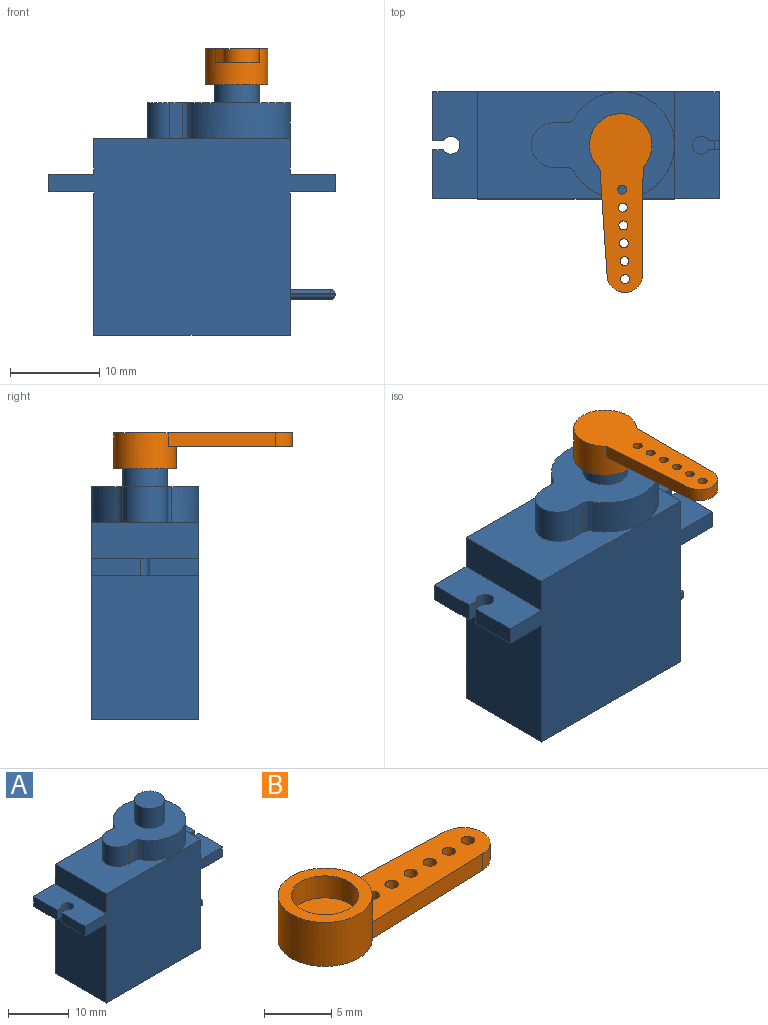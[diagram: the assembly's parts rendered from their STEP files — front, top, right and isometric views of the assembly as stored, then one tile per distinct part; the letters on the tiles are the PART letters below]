
ASSEMBLY  parts=2 mates=1
PART A: 50 faces, bbox 32x12x30 mm
  f0: plane 5.5x2mm, normal (1,0,0), area 11mm2, adj f8,f24,f25,f30
  f1: plane 5.5x2mm, normal (-1,0,0), area 11mm2, adj f2,f3,f8,f28
  f2: plane 12x5mm, normal (0,0,1), area 55.8mm2, adj f1,f8,f9,f10,f26,f27,f28,f29
  f3: plane 12x5mm, normal (0,0,-1), area 55.8mm2, adj f1,f4,f8,f10,f26,f27,f28,f29
  f4: plane 16x12mm, normal (-1,0,0), area 192mm2, adj f3,f8,f10,f13
  f5: plane 16x12mm, normal (1,0,0), area 188.4mm2, adj f8,f10,f13,f24,f33,f34,f35,f36
  f6: plane 16x12mm, normal (0,0,1), area 117.1mm2, adj f8,f9,f10,f14,f15,f16,f17,f21
  f7: plane 6x6mm, normal (0,0,1), area 7.7mm2, adj f10,f11,f14
  f8: plane 32x22mm, normal (0,1,0), area 504mm2, adj f0,f1,f2,f3,f4,f5,f6,f9
  f9: plane 12x4mm, normal (-1,0,0), area 48mm2, adj f2,f6,f8,f10
  f10: plane 32x22mm, normal (0,-1,0), area 504mm2, adj f2,f3,f4,f5,f6,f7,f9,f11
  f11: plane 12x4mm, normal (1,0,0), area 48mm2, adj f7,f8,f10,f12,f25
  f12: plane 6x6mm, normal (0,0,1), area 7.7mm2, adj f8,f11,f14
  f13: plane 22x12mm, normal (0,0,-1), area 264mm2, adj f4,f5,f8,f10
  f14: cylinder r=6mm len=12mm, axis (0,0,-1), area 125.7mm2, adj f6,f7,f12,f18,f21,f22
  f15: plane 4x1.44mm, normal (0,1,0), area 5.8mm2, adj f6,f16,f18,f21
  f16: cylinder r=2.5mm len=5mm, axis (0,0,-1), area 31.4mm2, adj f6,f15,f17,f18
  f17: plane 4x1.44mm, normal (0,-1,0), area 5.8mm2, adj f6,f16,f18,f22
  f18: plane 16x12mm, normal (0,0,1), area 111.8mm2, adj f14,f15,f16,f17,f19,f21,f22
  f19: cylinder r=2.5mm len=5mm, axis (0,0,-1), area 62.8mm2, adj f18,f20
  f20: plane 5x5mm, normal (0,0,1), area 19.6mm2, adj f19
  f21: cylinder r=1mm len=4mm, axis (0,0,-1), area 4.2mm2, adj f6,f14,f15,f18
  f22: cylinder r=1mm len=4mm, axis (0,0,-1), area 4.2mm2, adj f6,f14,f17,f18
  f23: plane 5.5x2mm, normal (1,0,0), area 11mm2, adj f10,f24,f25,f31
  f24: plane 12x5mm, normal (0,0,-1), area 55.8mm2, adj f0,f5,f8,f10,f23,f30,f31,f32
  f25: plane 12x5mm, normal (0,0,1), area 55.8mm2, adj f0,f8,f10,f11,f23,f30,f31,f32
  f26: plane 5.5x2mm, normal (-1,0,0), area 11mm2, adj f2,f3,f10,f29
  f27: cylinder r=1mm len=2mm, axis (0,0,1), area 10.5mm2, adj f2,f3,f28,f29
  f28: plane 2x1.13mm, normal (0,-1,0), area 2.3mm2, adj f1,f2,f3,f27
  f29: plane 2x1.13mm, normal (0,1,0), area 2.3mm2, adj f2,f3,f26,f27
  f30: plane 2x1.13mm, normal (0,-1,0), area 2.3mm2, adj f0,f24,f25,f32
  f31: plane 2x1.13mm, normal (0,1,0), area 2.3mm2, adj f23,f24,f25,f32
  f32: cylinder r=1mm len=2mm, axis (0,0,1), area 10.5mm2, adj f24,f25,f30,f31
  f33: plane 4.5x2.5mm, normal (0,0,1), area 11.2mm2, adj f5,f40,f46,f49
  f34: plane 4.5x0.1mm, normal (0,-1,0), area 0.5mm2, adj f5,f43,f47,f49
  f35: plane 4.5x2.5mm, normal (0,0,-1), area 11.2mm2, adj f5,f38,f42,f43
  f36: plane 4.5x0.1mm, normal (0,1,0), area 0.5mm2, adj f5,f38,f40,f41
  f37: plane 2.5x0.1mm, normal (1,0,0), area 0.3mm2, adj f41,f42,f46,f47
  f38: cylinder r=0.5mm len=4.5mm, axis (1,0,0), area 3.5mm2, adj f5,f35,f36,f39
  f39: sphere r=0.5mm, area 0.4mm2, adj f38,f41,f42
  f40: cylinder r=0.5mm len=4.5mm, axis (-1,0,0), area 3.5mm2, adj f5,f33,f36,f44
  f41: cylinder r=0.5mm len=0.5mm, axis (0,0,-1), area 0.1mm2, adj f36,f37,f39,f44
  f42: cylinder r=0.5mm len=2.5mm, axis (0,-1,0), area 2mm2, adj f35,f37,f39,f45
  f43: cylinder r=0.5mm len=4.5mm, axis (-1,0,0), area 3.5mm2, adj f5,f34,f35,f45
  f44: sphere r=0.5mm, area 0.4mm2, adj f40,f41,f46
  f45: sphere r=0.5mm, area 0.4mm2, adj f42,f43,f47
  f46: cylinder r=0.5mm len=2.5mm, axis (0,1,0), area 2mm2, adj f33,f37,f44,f48
  f47: cylinder r=0.5mm len=0.5mm, axis (0,0,1), area 0.1mm2, adj f34,f37,f45,f48
  f48: sphere r=0.5mm, area 0.4mm2, adj f46,f47,f49
  f49: cylinder r=0.5mm len=4.5mm, axis (1,0,0), area 3.5mm2, adj f5,f33,f34,f48
PART B: 15 faces, bbox 20x7x4 mm
  f0: plane 12.03x1.5mm, normal (0.03,-1,0), area 18.1mm2, adj f1,f9,f10,f11
  f1: cylinder r=2mm len=4mm, axis (0,0,-1), area 9.2mm2, adj f0,f2,f9,f10
  f2: plane 12.03x1.5mm, normal (0.03,1,0), area 18.1mm2, adj f1,f9,f10,f11
  f3: cylinder r=0.5mm len=1.5mm, axis (0,0,-1), area 4.7mm2, adj f9,f10
  f4: cylinder r=0.5mm len=1.5mm, axis (0,0,-1), area 4.7mm2, adj f9,f10
  f5: cylinder r=0.5mm len=1.5mm, axis (0,0,-1), area 4.7mm2, adj f9,f10
  f6: cylinder r=0.5mm len=1.5mm, axis (0,0,-1), area 4.7mm2, adj f9,f10
  f7: cylinder r=0.5mm len=1.5mm, axis (0,0,-1), area 4.7mm2, adj f9,f10
  f8: cylinder r=0.5mm len=1.5mm, axis (0,0,-1), area 4.7mm2, adj f9,f10
  f9: plane 13.97x4.83mm, normal (0,0,1), area 51.2mm2, adj f0,f1,f2,f3,f4,f5,f6,f7
  f10: plane 20x7mm, normal (0,0,-1), area 89.7mm2, adj f0,f1,f2,f3,f4,f5,f6,f7
  f11: cylinder r=3.5mm len=7mm, axis (0,0,-1), area 80mm2, adj f0,f2,f9,f10,f12
  f12: plane 7x7mm, normal (0,0,1), area 18.8mm2, adj f11,f13
  f13: cylinder r=2.5mm len=5mm, axis (0,0,1), area 31.4mm2, adj f12,f14
  f14: plane 5x5mm, normal (0,0,1), area 19.6mm2, adj f13
PLACE A t=(17.13,0.7,0)mm
PLACE B rot(axis=(0.72,-0.7,0),180deg) t=(23.25,-10.75,32)mm
MATE revolute B.f11 <-> A.f14  axis (0,0,-1) through (16,6,30)mm
